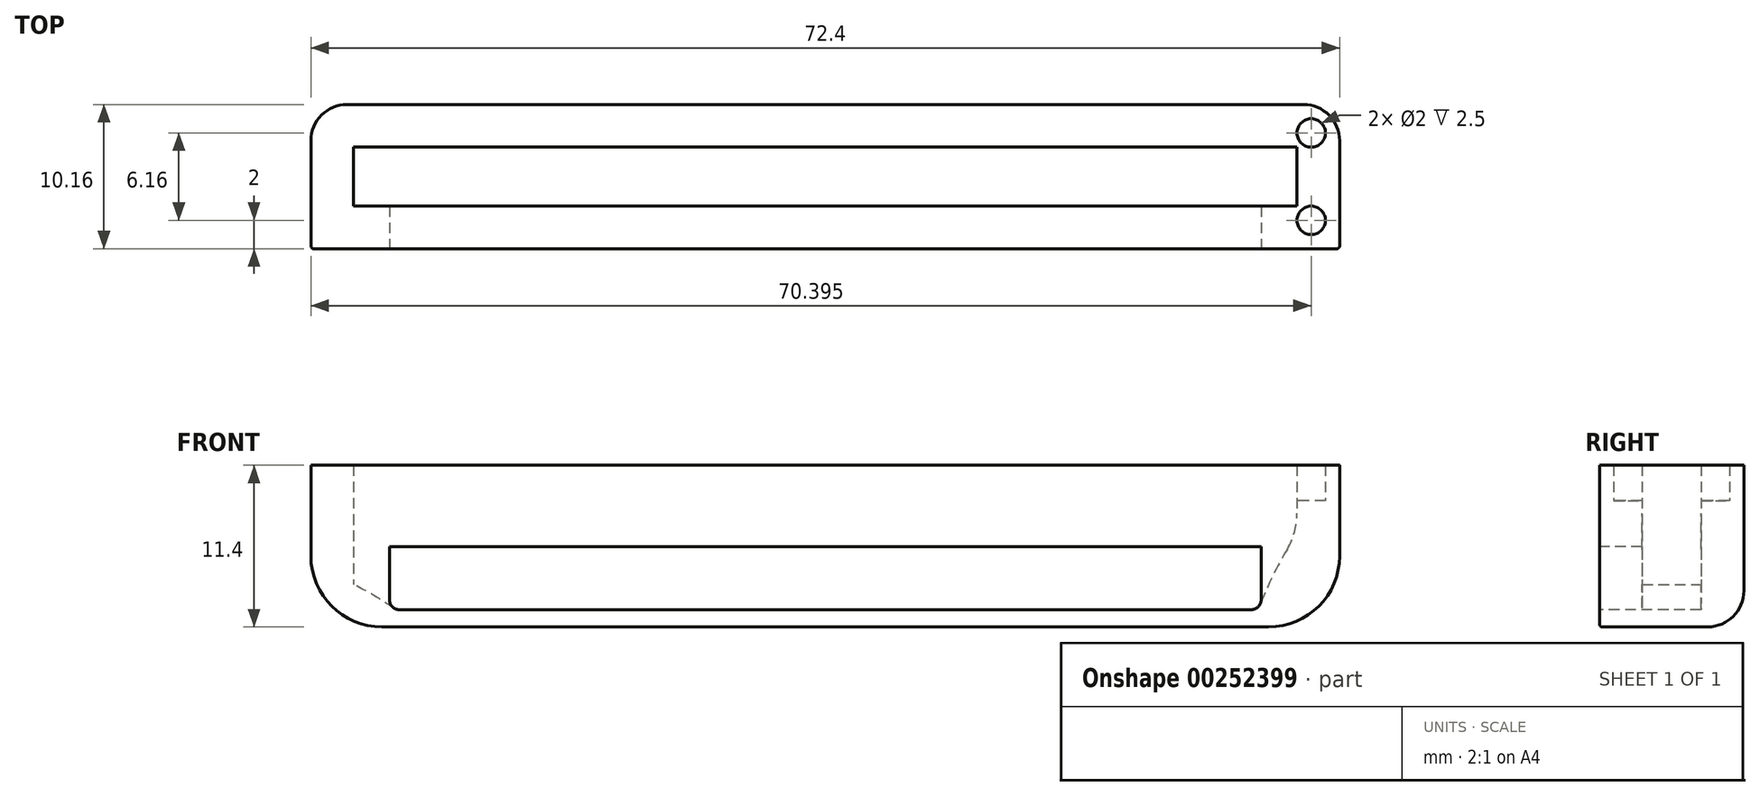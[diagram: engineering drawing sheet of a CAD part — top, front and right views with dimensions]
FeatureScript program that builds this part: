
annotation { "Feature Type Name" : "Feature", "Feature Type Description" : "" }
export const myFeature = defineFeature(function(context is Context, id is Id, definition is map)
    precondition{}
    {
        {
            var Q0;
            Q0=qCreatedBy(makeId("Front.planeOp"),FACE);
            var sketch = newSketch(context, id + "F0", { "sketchPlane" : qUnion([Q0])});
            skLineSegment(sketch, "E0.bottom", {"start": v(36.2, 4.45) * mm, "end": v(-36.2, 4.45) * mm});
            skLineSegment(sketch, "E0.top", {"start": v(36.2, -4.44) * mm, "end": v(-36.2, -4.44) * mm});
            skLineSegment(sketch, "E0.left", {"start": v(36.2, 4.45) * mm, "end": v(36.2, -4.44) * mm});
            skLineSegment(sketch, "E0.right", {"start": v(-36.2, 4.45) * mm, "end": v(-36.2, -4.44) * mm});
            skPoint(sketch, "E0.middle", {"position": v(0, 0) * mm});
            skSolve(sketch);
        }
        {
            var Q0;
            Q0=makeQuery(id+"F0.imprint","IMPRINT",FACE,{"disambiguationData":[TD([[makeQuery(id+"F0.imprint","IMPRINT",EDGE,{"derivedFrom":sQuery(id+"F0.wireOp",EDGE,"E0.bottom")}),1.0]])]});
            extrude(context, id + "F1", {"entities" : qUnion([Q0]), "depth" : 10.16 * mm});
        }
        {
            var Q0;
            Q0=makeQuery(id+"F1.opExtrude","SWEPT_FACE",FACE,{"disambiguationData":[OSD([sQuery(id+"F0.wireOp",EDGE,"E0.bottom")])]});
            shell(context, id + "F2", {"entities" : qUnion([Q0]), "thickness" : 3 * mm});
        }
        {
            var Q0;
            Q0=makeQuery(id+"F1.opExtrude","SWEPT_EDGE",EDGE,{"disambiguationData":[OSD([sQuery(id+"F0.wireOp",EDGE,"E0.top"),sQuery(id+"F0.wireOp",EDGE,"E0.right")])]});
            var Q1;
            Q1=makeQuery(id+"F1.opExtrude","SWEPT_EDGE",EDGE,{"disambiguationData":[OSD([sQuery(id+"F0.wireOp",EDGE,"E0.top"),sQuery(id+"F0.wireOp",EDGE,"E0.left")])]});
            var Q2;
            Q2=makeQuery(id+"F2.opShell","OFFSET_EDGE",EDGE,{"disambiguationData":[OSD([sQuery(id+"F0.wireOp",EDGE,"E0.top"),sQuery(id+"F0.wireOp",EDGE,"E0.left")])]});
            fillet(context, id + "F3", {"entities" : qUnion([Q0, Q1, Q2]), "radius" : 5 * mm, "tangentPropagation" : true, "allowEdgeOverflow" : false});
        }
        {
            var Q0;
            Q0=makeQuery(id+"F1.opExtrude","CAP_EDGE",EDGE,{"disambiguationData":[OSD([sQuery(id+"F0.wireOp",EDGE,"E0.top")])],"isStart":true});
            fillet(context, id + "F4", {"entities" : qUnion([Q0]), "radius" : 2.54 * mm, "tangentPropagation" : true, "allowEdgeOverflow" : false});
        }
        {
            var Q0;
            Q0=makeQuery(id+"F1.opExtrude","CAP_EDGE",EDGE,{"disambiguationData":[OSD([sQuery(id+"F0.wireOp",EDGE,"E0.top")])],"isStart":false});
            fillet(context, id + "F5", {"entities" : qUnion([Q0]), "radius" : 0.2 * mm, "tangentPropagation" : true, "allowEdgeOverflow" : false});
        }
        {
            var Q0;
            Q0=makeQuery(id+"F1.opExtrude","CAP_FACE",FACE,{"disambiguationData":[OSD([sQuery(id+"F0.wireOp",EDGE,"E0.bottom"),sQuery(id+"F0.wireOp",EDGE,"E0.top"),sQuery(id+"F0.wireOp",EDGE,"E0.left"),sQuery(id+"F0.wireOp",EDGE,"E0.right")])],"isStart":false});
            var sketch = newSketch(context, id + "F6", { "sketchPlane" : qUnion([Q0])});
            skLineSegment(sketch, "E1.bottom", {"start": v(30.67, 1.2) * mm, "end": v(-30.67, 1.2) * mm});
            skLineSegment(sketch, "E1.top", {"start": v(30.67, -3.23) * mm, "end": v(-30.67, -3.23) * mm});
            skLineSegment(sketch, "E1.left", {"start": v(30.67, 1.2) * mm, "end": v(30.67, -3.23) * mm});
            skLineSegment(sketch, "E1.right", {"start": v(-30.67, 1.2) * mm, "end": v(-30.67, -3.23) * mm});
            skPoint(sketch, "E1.middle", {"position": v(0, -1.02) * mm});
            skSolve(sketch);
        }
        {
            var Q0;
            Q0=makeQuery(id+"F6.imprint","IMPRINT",FACE,{"disambiguationData":[TD([[makeQuery(id+"F6.imprint","IMPRINT",EDGE,{"derivedFrom":sQuery(id+"F6.wireOp",EDGE,"E1.bottom")}),1.0]])]});
            extrude(context, id + "F7", {"entities" : qUnion([Q0]), "operationType" : NewBodyOperationType.REMOVE, "oppositeDirection" : true, "depth" : 2 * mm});
        }
        {
            var Q0;
            Q0=makeQuery(id+"F7.boolean.opBoolean","COPY",EDGE,{"derivedFrom":makeQuery(id+"F7.opExtrude","SWEPT_EDGE",EDGE,{"disambiguationData":[OSD([sQuery(id+"F6.wireOp",EDGE,"E1.top"),sQuery(id+"F6.wireOp",EDGE,"E1.left")])]})});
            var Q1;
            Q1=makeQuery(id+"F7.boolean.opBoolean","COPY",EDGE,{"derivedFrom":makeQuery(id+"F7.opExtrude","SWEPT_EDGE",EDGE,{"disambiguationData":[OSD([sQuery(id+"F6.wireOp",EDGE,"E1.top"),sQuery(id+"F6.wireOp",EDGE,"E1.right")])]})});
            fillet(context, id + "F8", {"entities" : qUnion([Q0, Q1]), "radius" : .7 * mm, "tangentPropagation" : true, "allowEdgeOverflow" : false});
        }
        {
            var Q0;
            Q0=makeQuery(id+"F1.opExtrude","SWEPT_FACE",FACE,{"disambiguationData":[OSD([sQuery(id+"F0.wireOp",EDGE,"E0.bottom")])]});
            var sketch = newSketch(context, id + "F9", { "sketchPlane" : qUnion([Q0])});
            skCircle(sketch, "E2", {"center": v(-34.2, -2) * mm, "radius": 1 * mm});
            skCircle(sketch, "E3.MirrorC", {"center": v(34.2, -2) * mm, "radius": 1 * mm});
            skCircle(sketch, "E4", {"center": v(-34.2, -8.16) * mm, "radius": 1 * mm});
            skCircle(sketch, "E5.MirrorC", {"center": v(34.2, -8.16) * mm, "radius": 1 * mm});
            skSolve(sketch);
        }
        {
            var Q0;
            Q0=makeQuery(id+"F9.imprint","IMPRINT",FACE,{"disambiguationData":[TD([[makeQuery(id+"F9.imprint","IMPRINT",EDGE,{"derivedFrom":sQuery(id+"F9.wireOp",EDGE,"E2")}),1.0]])]});
            var Q1;
            Q1=makeQuery(id+"F9.imprint","IMPRINT",FACE,{"disambiguationData":[TD([[makeQuery(id+"F9.imprint","IMPRINT",EDGE,{"derivedFrom":sQuery(id+"F9.wireOp",EDGE,"E4")}),1.0]])]});
            var Q2;
            Q2=makeQuery(id+"F9.imprint","IMPRINT",FACE,{"disambiguationData":[TD([[makeQuery(id+"F9.imprint","IMPRINT",EDGE,{"derivedFrom":sQuery(id+"F9.wireOp",EDGE,"E3.MirrorC")}),-1.0]])]});
            var Q3;
            Q3=makeQuery(id+"F9.imprint","IMPRINT",FACE,{"disambiguationData":[TD([[makeQuery(id+"F9.imprint","IMPRINT",EDGE,{"derivedFrom":sQuery(id+"F9.wireOp",EDGE,"E5.MirrorC")}),-1.0]])]});
            extrude(context, id + "F10", {"entities" : qUnion([Q0, Q1, Q2, Q3]), "operationType" : NewBodyOperationType.ADD, "depth" : 2.5 * mm});
        }
        {
            var Q0;
            Q0=makeQuery(id+"F7.boolean.opBoolean","COPY",FACE,{"derivedFrom":makeQuery(id+"F7.opExtrude","CAP_FACE",FACE,{"disambiguationData":[OSD([sQuery(id+"F6.wireOp",EDGE,"E1.bottom"),sQuery(id+"F6.wireOp",EDGE,"E1.top"),sQuery(id+"F6.wireOp",EDGE,"E1.left"),sQuery(id+"F6.wireOp",EDGE,"E1.right")])],"isStart":false})});
            extrude(context, id + "F11", {"entities" : qUnion([Q0]), "operationType" : NewBodyOperationType.REMOVE, "oppositeDirection" : true, "depth" : 5.16 * mm});
        }
        {
            var Q0;
            Q0=makeQuery(id+"F11.boolean.opBoolean","INTERSECT",EDGE,{"derivedFrom":[makeQuery(id+"F2.opShell","OFFSET_FACE",FACE,{"disambiguationData":[OSD([sQuery(id+"F0.wireOp",EDGE,"E0.top")])]}),makeQuery(id+"F11.opExtrude","SWEPT_FACE",FACE,{"disambiguationData":[OSD([sQuery(id+"F6.wireOp",EDGE,"E1.right")])]})]});
            var Q1;
            {var subQ0=sQuery(id+"F0.wireOp",EDGE,"E0.left");var subQ1=sQuery(id+"F0.wireOp",EDGE,"E0.top");Q1=makeQuery(id+"F11.boolean.opBoolean","INTERSECT",EDGE,{"derivedFrom":[makeQuery(id+"F3.opFillet","BLEND_FACE",FACE,{"disambiguationData":[OSD([subQ1,subQ0]),TDD([makeQuery(id+"F2.opShell","OFFSET_EDGE",EDGE,{"disambiguationData":[OSD([subQ1,subQ0])]})])]}),makeQuery(id+"F11.opExtrude","SWEPT_FACE",FACE,{"disambiguationData":[OSD([sQuery(id+"F6.wireOp",EDGE,"E1.left")])]})]});}
            fillet(context, id + "F12", {"entities" : qUnion([Q0, Q1]), "radius" : 30 * mm, "tangentPropagation" : true, "allowEdgeOverflow" : false});
        }
    });
